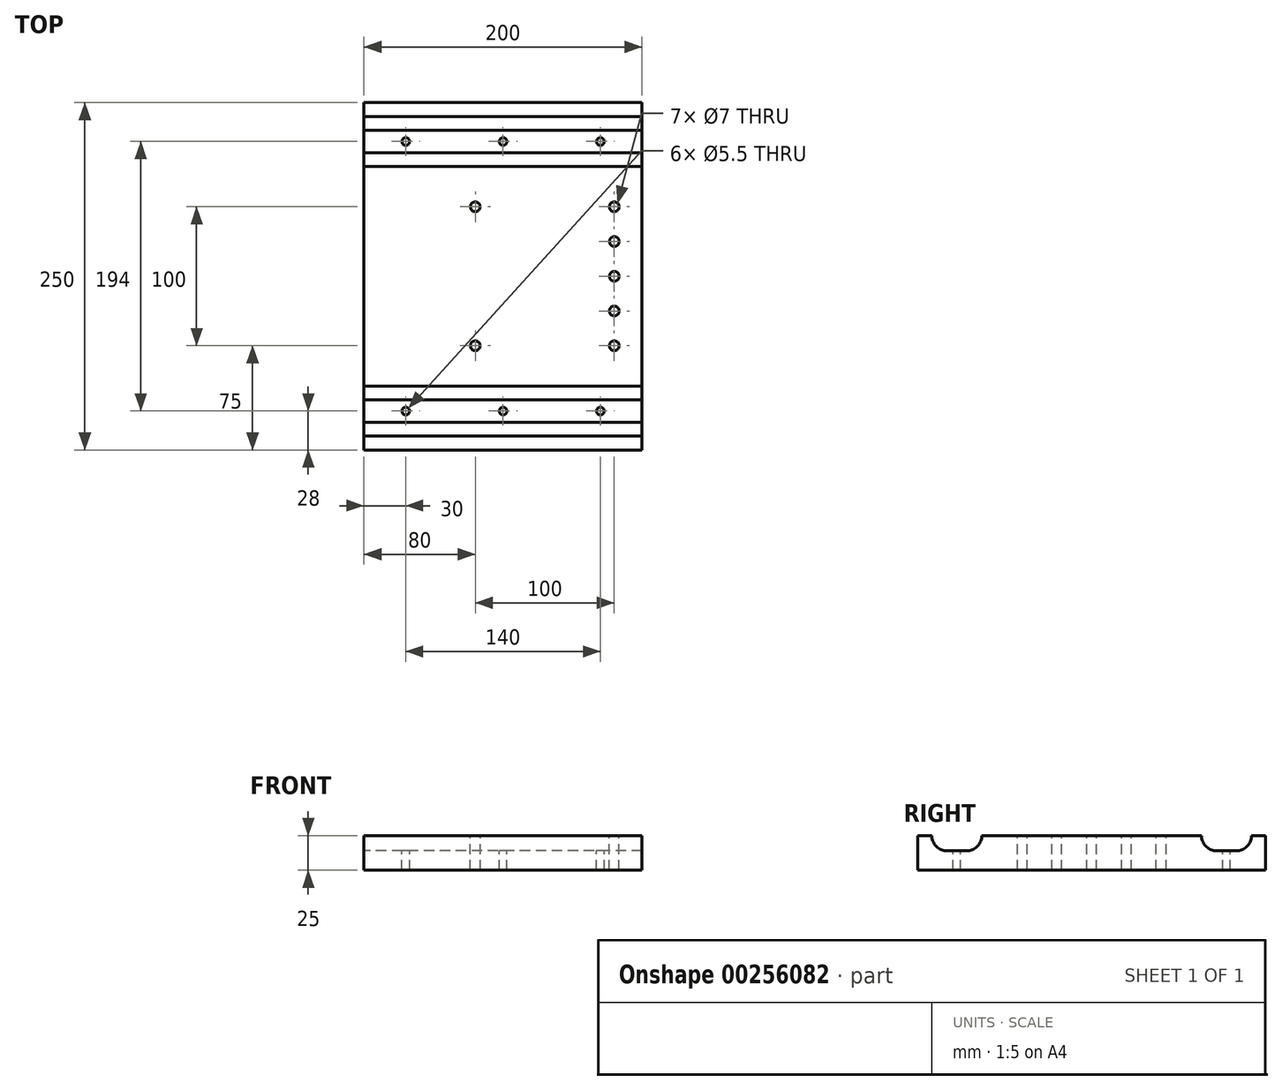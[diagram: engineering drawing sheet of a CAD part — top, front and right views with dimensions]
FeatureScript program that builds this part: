
annotation { "Feature Type Name" : "Feature", "Feature Type Description" : "" }
export const myFeature = defineFeature(function(context is Context, id is Id, definition is map)
    precondition{}
    {
        {
            var Q0;
            Q0=qCreatedBy(makeId("Top.planeOp"),FACE);
            var sketch = newSketch(context, id + "F0", { "sketchPlane" : qUnion([Q0])});
            skLineSegment(sketch, "E0.bottom", {"start": v(50, 50) * mm, "end": v(-50, 50) * mm, "construction": true});
            skLineSegment(sketch, "E0.top", {"start": v(50, -50) * mm, "end": v(-50, -50) * mm, "construction": true});
            skLineSegment(sketch, "E0.left", {"start": v(50, 50) * mm, "end": v(50, -50) * mm, "construction": true});
            skLineSegment(sketch, "E0.right", {"start": v(-50, 50) * mm, "end": v(-50, -50) * mm, "construction": true});
            skPoint(sketch, "E0.middle", {"position": v(0, 0) * mm});
            skCircle(sketch, "E1", {"center": v(-50, 50) * mm, "radius": 3.5 * mm});
            skCircle(sketch, "E2", {"center": v(-50, -50) * mm, "radius": 3.5 * mm});
            skCircle(sketch, "E3", {"center": v(50, 50) * mm, "radius": 3.5 * mm});
            skCircle(sketch, "E4.0.1.0", {"center": v(50, 25) * mm, "radius": 3.5 * mm});
            skCircle(sketch, "E4.0.2.0", {"center": v(50, 0) * mm, "radius": 3.5 * mm});
            skCircle(sketch, "E4.0.3.0", {"center": v(50, -25) * mm, "radius": 3.5 * mm});
            skCircle(sketch, "E4.0.4.0", {"center": v(50, -50) * mm, "radius": 3.5 * mm});
            skLineSegment(sketch, "E4.direction1", {"start": v(50, 50) * mm, "end": v(75, 50) * mm, "construction": true});
            skLineSegment(sketch, "E4.direction2", {"start": v(50, 50) * mm, "end": v(50, 25) * mm, "construction": true});
            skLineSegment(sketch, "E5.bottom", {"start": v(70, 125) * mm, "end": v(-130, 125) * mm});
            skLineSegment(sketch, "E5.top", {"start": v(70, -125) * mm, "end": v(-130, -125) * mm});
            skLineSegment(sketch, "E5.left", {"start": v(70, 125) * mm, "end": v(70, -125) * mm});
            skLineSegment(sketch, "E5.right", {"start": v(-130, 125) * mm, "end": v(-130, -125) * mm});
            skLineSegment(sketch, "E6", {"start": v(50, 0) * mm, "end": v(70, 0) * mm, "construction": true});
            skLineSegment(sketch, "E7.bottom", {"start": v(-130, -115) * mm, "end": v(70, -115) * mm});
            skLineSegment(sketch, "E7.top", {"start": v(-130, -79) * mm, "end": v(70, -79) * mm});
            skLineSegment(sketch, "E7.left", {"start": v(-130, -115) * mm, "end": v(-130, -79) * mm});
            skLineSegment(sketch, "E7.right", {"start": v(70, -115) * mm, "end": v(70, -79) * mm});
            skLineSegment(sketch, "E8.MirrorCS", {"start": v(-130, 79) * mm, "end": v(70, 79) * mm});
            skLineSegment(sketch, "E9.MirrorCS", {"start": v(-130, 115) * mm, "end": v(70, 115) * mm});
            skLineSegment(sketch, "E10", {"start": v(-130, -97) * mm, "end": v(-30, -97) * mm, "construction": true});
            skCircle(sketch, "E11", {"center": v(-30, -97) * mm, "radius": 2.75 * mm});
            skLineSegment(sketch, "E12", {"start": v(-30, -115) * mm, "end": v(-30, -79) * mm, "construction": true});
            skLineSegment(sketch, "E13", {"start": v(-30, -97) * mm, "end": v(70, -97) * mm, "construction": true});
            skCircle(sketch, "E14", {"center": v(40, -97) * mm, "radius": 2.75 * mm});
            skCircle(sketch, "E15.MirrorC", {"center": v(-100, -97) * mm, "radius": 2.75 * mm});
            skCircle(sketch, "E16.MirrorC", {"center": v(40, 97) * mm, "radius": 2.75 * mm});
            skCircle(sketch, "E17.MirrorC", {"center": v(-30, 97) * mm, "radius": 2.75 * mm});
            skCircle(sketch, "E18.MirrorC", {"center": v(-100, 97) * mm, "radius": 2.75 * mm});
            skSolve(sketch);
        }
        {
            var Q0;
            Q0 = qSketchRegion(id + "F0", true);
            extrude(context, id + "F1", {"entities" : qUnion([Q0]), "oppositeDirection" : true, "depth" : 25 * mm});
        }
        {
            var Q0;
            Q0=makeQuery(id+"F1.opExtrude","SWEPT_FACE",FACE,{"disambiguationData":[OSD([sQuery(id+"F0.wireOp",EDGE,"E5.right"),sQuery(id+"F0.wireOp",EDGE,"E7.left")])]});
            var sketch = newSketch(context, id + "F2", { "sketchPlane" : qUnion([Q0])});
            skPoint(sketch, "E19.0", {"position": v(-115, 0) * mm});
            skPoint(sketch, "E20.0", {"position": v(-79, 0) * mm});
            skLineSegment(sketch, "E21", {"start": v(-115, 0) * mm, "end": v(-79, 0) * mm});
            skLineSegment(sketch, "E22", {"start": v(-97, 0) * mm, "end": v(-97, -11) * mm, "construction": true});
            skLineSegment(sketch, "E23", {"start": v(-115, -11) * mm, "end": v(-105, -11) * mm, "construction": true});
            skPoint(sketch, "E24", {"position": v(-105, -11) * mm});
            skArc(sketch, "E25", {"start": v(-115, 0) * mm, "mid": v(-112.13, -7.43) * mm, "end": v(-105, -11) * mm});
            skArc(sketch, "E26.MirrorCS", {"start": v(-79, 0) * mm, "mid": v(-81.87, -7.43) * mm, "end": v(-89, -11) * mm});
            skLineSegment(sketch, "E27", {"start": v(0, 0) * mm, "end": v(0, -25) * mm, "construction": true});
            skArc(sketch, "E28.MirrorCS", {"start": v(79, 0) * mm, "mid": v(81.87, -7.43) * mm, "end": v(89, -11) * mm});
            skArc(sketch, "E29.MirrorCS", {"start": v(115, 0) * mm, "mid": v(112.13, -7.43) * mm, "end": v(105, -11) * mm});
            skLineSegment(sketch, "E30", {"start": v(-105, -11) * mm, "end": v(-89, -11) * mm});
            skLineSegment(sketch, "E31", {"start": v(-89, -11) * mm, "end": v(-79, -11) * mm, "construction": true});
            skLineSegment(sketch, "E32.MirrorCS", {"start": v(105, -11) * mm, "end": v(89, -11) * mm});
            skLineSegment(sketch, "E33.MirrorCS", {"start": v(115, 0) * mm, "end": v(79, 0) * mm});
            skSolve(sketch);
        }
        {
            var Q0;
            Q0 = qSketchRegion(id + "F2", true);
            extrude(context, id + "F3", {"entities" : qUnion([Q0]), "operationType" : NewBodyOperationType.REMOVE, "endBound" : BoundingType.THROUGH_ALL, "oppositeDirection" : true, "depth" : 25 * mm});
        }
    });
